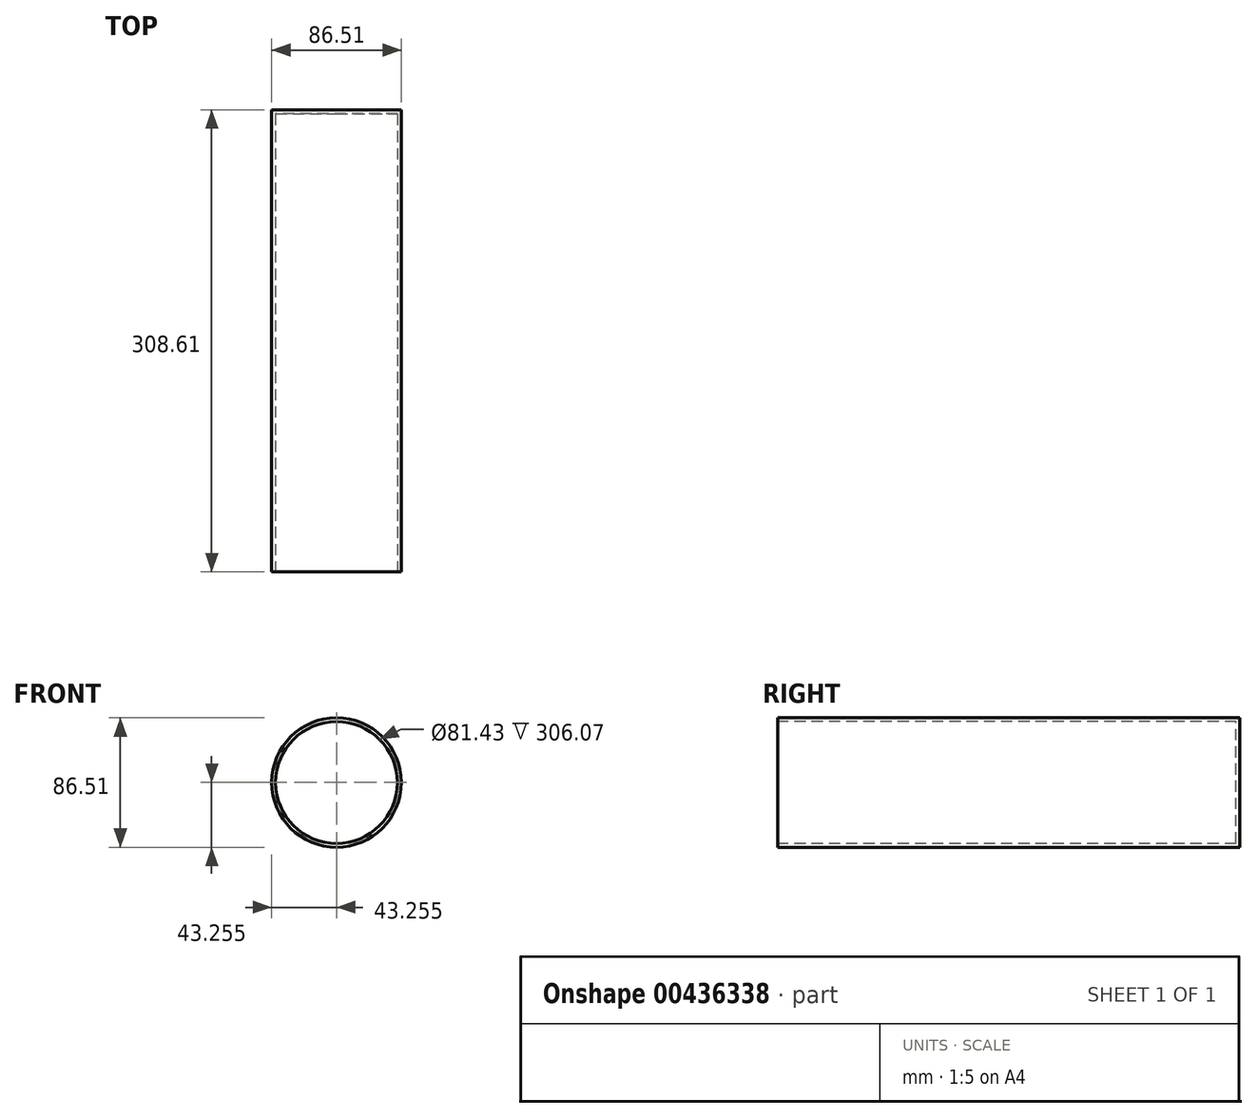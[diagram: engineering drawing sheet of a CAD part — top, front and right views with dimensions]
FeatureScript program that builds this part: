
annotation { "Feature Type Name" : "Feature", "Feature Type Description" : "" }
export const myFeature = defineFeature(function(context is Context, id is Id, definition is map)
    precondition{}
    {
        {
            var Q0;
            Q0=qCreatedBy(makeId("Front.planeOp"),FACE);
            var sketch = newSketch(context, id + "F0", { "sketchPlane" : qUnion([Q0])});
            skCircle(sketch, "E0", {"center": v(-215.85, -11.33) * mm, "radius": 43.26 * mm});
            skSolve(sketch);
        }
        {
            var Q0;
            Q0=makeQuery(id+"F0.imprint","IMPRINT",FACE,{"disambiguationData":[TD([[makeQuery(id+"F0.imprint","IMPRINT",EDGE,{"derivedFrom":sQuery(id+"F0.wireOp",EDGE,"E0")}),1.0]])]});
            extrude(context, id + "F1", {"entities" : qUnion([Q0]), "oppositeDirection" : true, "depth" : 308.6 * mm});
        }
        {
            var Q0;
            Q0=qCreatedBy(makeId("Front.planeOp"),FACE);
            var sketch = newSketch(context, id + "F2", { "sketchPlane" : qUnion([Q0])});
            skArc(sketch, "E1", {"start": v(0, 18.42) * mm, "mid": v(-18.42, 0) * mm, "end": v(0, -18.42) * mm});
            skSolve(sketch);
        }
        {
            var Q0;
            Q0=makeQuery(id+"F1.opExtrude","CAP_FACE",FACE,{"disambiguationData":[OSD([sQuery(id+"F0.wireOp",EDGE,"E0")])],"isStart":true});
            shell(context, id + "F3", {"entities" : qUnion([Q0]), "thickness" : 2.54 * mm});
        }
        {
            var Q0;
            Q0=qCreatedBy(makeId("Front.planeOp"),FACE);
            var sketch = newSketch(context, id + "F4", { "sketchPlane" : qUnion([Q0])});
            skLineSegment(sketch, "E2", {"start": v(0, 0) * mm, "end": v(0, -18.22) * mm});
            skSolve(sketch);
        }
        {
            var Q0;
            Q0=sQuery(id+"F2.wireOp",EDGE,"E1");
            var Q1;
            Q1=sQuery(id+"F4.wireOp",EDGE,"E2");
            revolve(context, id + "F5", {"bodyType" : ToolBodyType.SURFACE, "surfaceEntities" : qUnion([Q0]), "axis" : qUnion([Q1]), "revolveType" : RevolveType.FULL});
        }
    });
